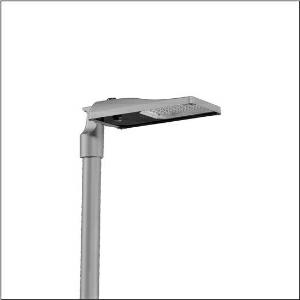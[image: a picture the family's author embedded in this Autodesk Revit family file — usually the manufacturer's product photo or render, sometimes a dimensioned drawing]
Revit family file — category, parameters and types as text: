
# Revit family: streetlight_sl_31_mini___st0_5a_5xh2b4at08ha_3879
name_source: partatom
category: Lighting Fixtures
units: mm (PartAtom-declared; Revit-internal decimal feet)

## family parameters
Cut with Voids When Loaded = No
Host = Face
Light Source = No
Part Type = Normal
Room Calculation Point = No
Round Connector Dimension = Use Diameter
Shared = No

## types (1)
- --- (1 x LED, 9560 lm, 68.3 W, 4000K)
    Apparent Load = 68 VA
    CIE Flux Codes = 41 75 97 100 100
    Color Rendering = 70
    Color Temperature = 4000K
    Default Elevation = 1800 mm
    Description = Streetlight SL 31 mini D4i mast luminaire for post-top, side-entry; light control with lens of PMMA; light distribution: ST0.5a, direct asymmetric distribution, for standard-compliant lighting for roads and squares; LED: luminous flux: 9.560lm, light colour: 740, colour temperature: 4000K; luminous efficacy: 140lm/W; control: pre-setting: logarithmic dimming characteristic, flexible luminous flux parameterisation, time-dependent luminous flux control, constant luminous flux control, power reduction, intelligent temperature release in ECG and LED module, overheat protection; luminaire housing, of diecast aluminium, Siteco® metallic grey (DB 702S), corrosivity category C5 high according to DIN EN ISO 12944; cover of toughened safety glass, transparent, mast flange of diecast aluminium, Siteco® metallic grey (DB 702S), spigot size: 76/60mm, mast flange included unmounted; with cable H07RN-F 2x 1.5mm², cable length: 8,5m, connection cable pre-assembled; mains connection: 220..240V, AC, 50/60Hz; power consumption (at start of service life): 68,3W / (at end of service life): 74,5W / (with reduced operation 50%): 29,5W; protection rating (complete): IP66; insulation class (complete): insulation class II (safety insulation); impact resistance: IK09; certification: CE, ENEC, ENEC+, VDE, UKCA, ZD4i; permissible operating ambient temperature for outdoor applications: -40..+50°C; packaging unit: 1 piece

Light Distribution: ST0.5a
    Height = 76 mm
    Lamp = 1 x LED
    Lamp Light Flux = 9560 lm
    Lamp Power = 68.3 W
    Lamp count = 1
    Length = 547 mm
    Luminous efficacy = 140 lm/W
    Manufacturer = Siteco
    ModVariant = No
    Model = 5XH2B4AT08HA
    Number of Poles = 1
    OnlyDefault = Yes
    Power Factor = 1
    Product Name = Streetlight SL 31 mini | ST0.5a
    Product group = mast luminaire | pylon top
    ProductGroupID = 6100
    Protection Class = Protection class II
    Protection Degree = IP 66
    RLX_Detail_Level = 1
    RLX_Emergency_Light_Flux = 0 lm
    RLX_Emergency_Type = 0
    RLX_Emergency_Type_DB = No
    RlxData = <blob elided: 35253 chars, md5=8c4f6cbe>
    Socket = socket
    Standby Power = 0 W
    System Light Flux = 9560 lm
    System Power = 68 W
    Type Comments = factory setting: luminous flux: 100 % | dim-lin: 254 | 692 mA
    Type Image = l_1300332.jpg
    URL = http://relux.com
    VarID = @adj_002515
    Voltage = 0 V
    Weight = 0.00 kg
    Width = 265 mm

## geometry (parser evidence)
native form markers: Blend x4, Sweep x12
no freeform markers — native parametric forms only
